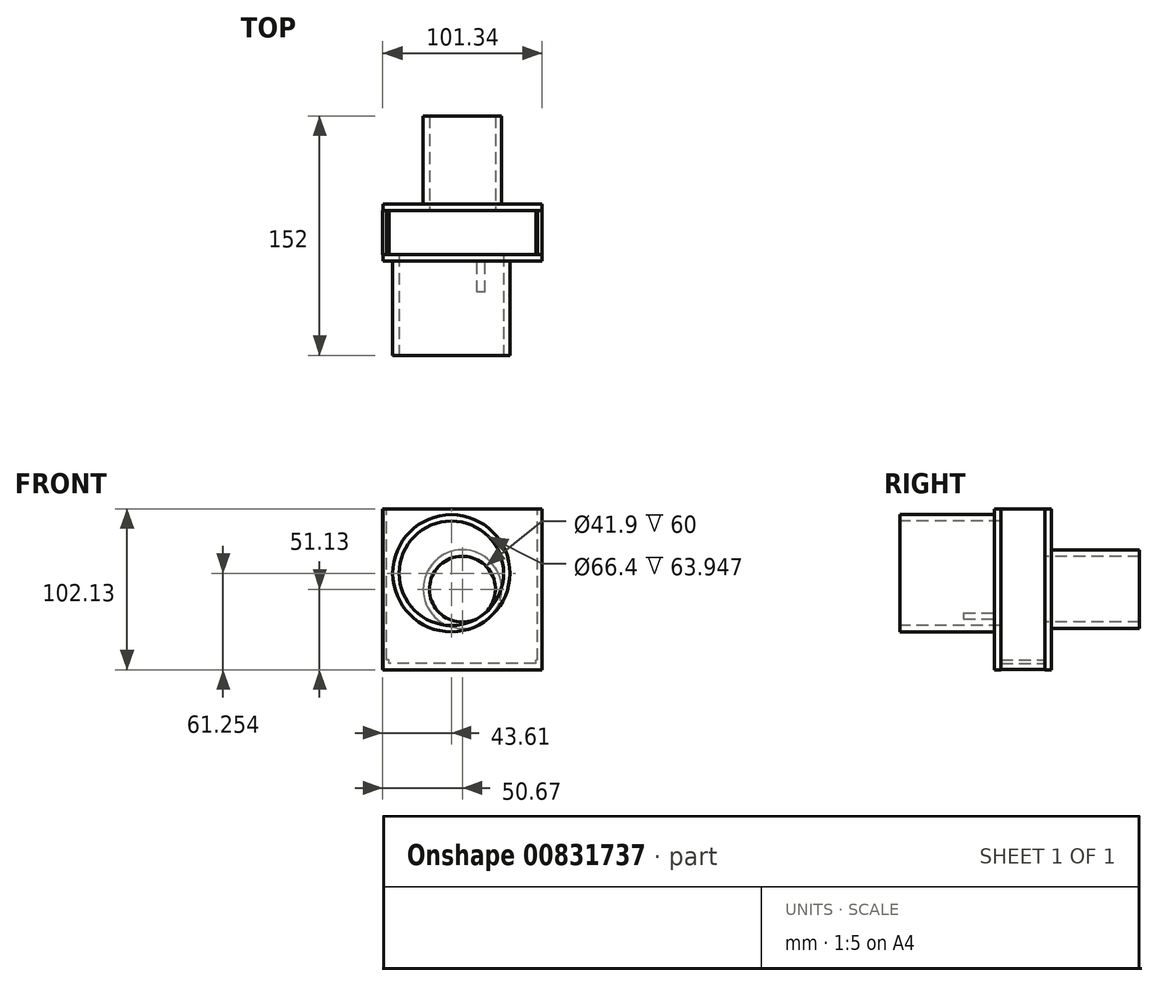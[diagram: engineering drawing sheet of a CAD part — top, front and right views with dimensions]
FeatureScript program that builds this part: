
annotation { "Feature Type Name" : "Feature", "Feature Type Description" : "" }
export const myFeature = defineFeature(function(context is Context, id is Id, definition is map)
    precondition{}
    {
        {
            var Q0;
            Q0=qCreatedBy(makeId("Front.planeOp"),FACE);
            var sketch = newSketch(context, id + "F0", { "sketchPlane" : qUnion([Q0])});
            skLineSegment(sketch, "E0.bottom", {"start": v(46.67, -47) * mm, "end": v(-46.67, -47) * mm});
            skLineSegment(sketch, "E0.top", {"start": v(46.67, 47) * mm, "end": v(-46.67, 47) * mm});
            skLineSegment(sketch, "E0.left", {"start": v(46.67, -47) * mm, "end": v(46.67, 47) * mm});
            skLineSegment(sketch, "E0.right", {"start": v(-46.67, -47) * mm, "end": v(-46.67, 47) * mm});
            skPoint(sketch, "E0.middle", {"position": v(0, 0) * mm});
            skLineSegment(sketch, "E1.0", {"start": v(50.67, 51) * mm, "end": v(-50.67, 51) * mm});
            skLineSegment(sketch, "E1.1", {"start": v(50.67, -51) * mm, "end": v(50.67, 51) * mm});
            skLineSegment(sketch, "E1.2", {"start": v(50.67, -51) * mm, "end": v(-50.67, -51) * mm});
            skLineSegment(sketch, "E1.3", {"start": v(-50.67, -51) * mm, "end": v(-50.67, 51) * mm});
            skSolve(sketch);
        }
        {
            var Q0;
            Q0=makeQuery(id+"F0.imprint","IMPRINT",FACE,{"disambiguationData":[TD([[makeQuery(id+"F0.imprint","IMPRINT",EDGE,{"derivedFrom":sQuery(id+"F0.wireOp",EDGE,"E0.bottom")}),1.0]])]});
            extrude(context, id + "F1", {"entities" : qUnion([Q0]), "depth" : 28 * mm, "offsetDistance" : 25 * mm});
        }
        {
            var Q0;
            Q0=qCreatedBy(makeId("Right.planeOp"),FACE);
            var sketch = newSketch(context, id + "F2", { "sketchPlane" : qUnion([Q0])});
            skLineSegment(sketch, "E2.bottom", {"start": v(-32, 50.87) * mm, "end": v(4, 50.87) * mm});
            skLineSegment(sketch, "E2.top", {"start": v(-32, -51.13) * mm, "end": v(4, -51.13) * mm});
            skLineSegment(sketch, "E2.left", {"start": v(-32, 50.87) * mm, "end": v(-32, -51.13) * mm});
            skLineSegment(sketch, "E2.right", {"start": v(4, 50.87) * mm, "end": v(4, -51.13) * mm});
            skLineSegment(sketch, "E3", {"start": v(-28.05, 50.87) * mm, "end": v(-28.05, -51.13) * mm});
            skLineSegment(sketch, "E4", {"start": v(-28.05, -51.13) * mm, "end": v(0, -51.13) * mm});
            skPoint(sketch, "E4.endSnap0", {"position": v(-14, -51.13) * mm});
            skLineSegment(sketch, "E5", {"start": v(0, -51.13) * mm, "end": v(0, 50.87) * mm});
            skSolve(sketch);
        }
        {
            var Q0;
            {var subQ0=sQuery(id+"F2.wireOp",EDGE,"E2.left");Q0=makeQuery(id+"F2.imprint","IMPRINT",FACE,{"disambiguationData":[TD([[makeQuery(id+"F2.imprint","IMPRINT",EDGE,{"derivedFrom":subQ0}),1.0]])]});}
            var Q1;
            {var subQ0=sQuery(id+"F2.wireOp",EDGE,"E2.right");Q1=makeQuery(id+"F2.imprint","IMPRINT",FACE,{"disambiguationData":[TD([[makeQuery(id+"F2.imprint","IMPRINT",EDGE,{"derivedFrom":subQ0}),-1.0]])]});}
            extrude(context, id + "F3", {"entities" : qUnion([Q0, Q1]), "depth" : 50.4 * mm, "offsetDistance" : 25 * mm, "hasSecondDirection" : true, "secondDirectionOppositeDirection" : true, "secondDirectionDepth" : 50.3 * mm});
        }
        {
            var Q0;
            Q0=makeQuery(id+"F1.opExtrude","SWEPT_FACE",FACE,{"disambiguationData":[OSD([sQuery(id+"F0.wireOp",EDGE,"E1.0")])]});
            var sketch = newSketch(context, id + "F4", { "sketchPlane" : qUnion([Q0])});
            skLineSegment(sketch, "E6.bottom", {"start": v(-48.2, 0) * mm, "end": v(47.8, 0) * mm});
            skLineSegment(sketch, "E6.top", {"start": v(-48.2, -28) * mm, "end": v(47.8, -28) * mm});
            skLineSegment(sketch, "E6.left", {"start": v(-48.2, 0) * mm, "end": v(-48.2, -28) * mm});
            skLineSegment(sketch, "E6.right", {"start": v(47.8, 0) * mm, "end": v(47.8, -28) * mm});
            skSolve(sketch);
        }
        {
            var Q0;
            Q0=makeQuery(id+"F4.imprint","IMPRINT",FACE,{"disambiguationData":[TD([[makeQuery(id+"F4.imprint","IMPRINT",EDGE,{"derivedFrom":sQuery(id+"F4.wireOp",EDGE,"E6.bottom")}),1.0]])]});
            extrude(context, id + "F5", {"entities" : qUnion([Q0]), "operationType" : NewBodyOperationType.REMOVE, "oppositeDirection" : true, "depth" : 96 * mm, "offsetDistance" : 25 * mm});
        }
        {
            var Q0;
            Q0=makeQuery(id+"F3.opExtrude","SWEPT_FACE",FACE,{"disambiguationData":[OSD([sQuery(id+"F2.wireOp",EDGE,"E2.left")])]});
            var sketch = newSketch(context, id + "F6", { "sketchPlane" : qUnion([Q0])});
            skLineSegment(sketch, "E7", {"start": v(-7.06, 50.87) * mm, "end": v(-7.06, -51.13) * mm});
            skLineSegment(sketch, "E8", {"start": v(-50.3, 10.12) * mm, "end": v(50.4, 10.12) * mm});
            skCircle(sketch, "E9", {"center": v(-7.06, 10.12) * mm, "radius": 33.25 * mm});
            skCircle(sketch, "E10.0", {"center": v(-7.06, 10.12) * mm, "radius": 37.25 * mm});
            skCircle(sketch, "E11", {"center": v(-7.06, 10.12) * mm, "radius": 33.2 * mm});
            skSolve(sketch);
        }
        {
            var Q0;
            {var subQ0=sQuery(id+"F6.wireOp",EDGE,"E11");var subQ1=sQuery(id+"F6.wireOp",EDGE,"E7");var subQ2=makeQuery(id+"F6.imprint","INTERSECT",VERTEX,{"disambiguationData":[OD(0.0)],"derivedFrom":[subQ1,subQ0]});Q0=makeQuery(id+"F6.imprint","IMPRINT",FACE,{"disambiguationData":[TD([[makeQuery(id+"F6.imprint","IMPRINT",EDGE,{"disambiguationData":[TD([[subQ2,-1.0]])],"derivedFrom":subQ1}),-1.0]])]});}
            var Q1;
            {var subQ0=sQuery(id+"F6.wireOp",EDGE,"E11");var subQ1=sQuery(id+"F6.wireOp",EDGE,"E7");var subQ2=makeQuery(id+"F6.imprint","INTERSECT",VERTEX,{"disambiguationData":[OD(0.0)],"derivedFrom":[subQ1,subQ0]});Q1=makeQuery(id+"F6.imprint","IMPRINT",FACE,{"disambiguationData":[TD([[makeQuery(id+"F6.imprint","IMPRINT",EDGE,{"disambiguationData":[TD([[subQ2,-1.0]])],"derivedFrom":subQ1}),1.0]])]});}
            var Q2;
            {var subQ0=sQuery(id+"F6.wireOp",EDGE,"E8");var subQ1=sQuery(id+"F6.wireOp",EDGE,"E7");var subQ2=makeQuery(id+"F6.imprint","INTERSECT",VERTEX,{"derivedFrom":[subQ1,subQ0]});Q2=makeQuery(id+"F6.imprint","IMPRINT",FACE,{"disambiguationData":[TD([[makeQuery(id+"F6.imprint","IMPRINT",EDGE,{"disambiguationData":[TD([[subQ2,-1.0]])],"derivedFrom":subQ1}),1.0]])]});}
            var Q3;
            {var subQ0=sQuery(id+"F6.wireOp",EDGE,"E8");var subQ1=sQuery(id+"F6.wireOp",EDGE,"E7");var subQ2=makeQuery(id+"F6.imprint","INTERSECT",VERTEX,{"derivedFrom":[subQ1,subQ0]});Q3=makeQuery(id+"F6.imprint","IMPRINT",FACE,{"disambiguationData":[TD([[makeQuery(id+"F6.imprint","IMPRINT",EDGE,{"disambiguationData":[TD([[subQ2,-1.0]])],"derivedFrom":subQ1}),-1.0]])]});}
            extrude(context, id + "F7", {"entities" : qUnion([Q0, Q1, Q2, Q3]), "operationType" : NewBodyOperationType.REMOVE, "oppositeDirection" : true, "depth" : 5 * mm, "offsetDistance" : 25 * mm});
        }
        {
            var Q0;
            Q0=makeQuery(id+"F3.opExtrude","SWEPT_FACE",FACE,{"disambiguationData":[OSD([sQuery(id+"F2.wireOp",EDGE,"E2.left")])]});
            var sketch = newSketch(context, id + "F8", { "sketchPlane" : qUnion([Q0])});
            skCircle(sketch, "E12.0", {"center": v(-7.06, 10.12) * mm, "radius": 37.2 * mm});
            skSolve(sketch);
        }
        {
            var Q0;
            Q0=makeQuery(id+"F8.imprint","IMPRINT",FACE,{"disambiguationData":[TD([[makeQuery(id+"F8.imprint","IMPRINT",EDGE,{"derivedFrom":sQuery(id+"F8.wireOp",EDGE,"E12.0")}),1.0]])]});
            extrude(context, id + "F9", {"entities" : qUnion([Q0]), "operationType" : NewBodyOperationType.ADD, "depth" : 60 * mm, "offsetDistance" : 25 * mm});
        }
        {
            var Q0;
            Q0=qCreatedBy(makeId("Front.planeOp"),FACE);
            var sketch = newSketch(context, id + "F10", { "sketchPlane" : qUnion([Q0])});
            skCircle(sketch, "E13", {"center": v(0, 0) * mm, "radius": 24.95 * mm});
            skCircle(sketch, "E14.0", {"center": v(0, 0) * mm, "radius": 20.95 * mm});
            skCircle(sketch, "E15", {"center": v(0, 0) * mm, "radius": 18.2 * mm});
            skSolve(sketch);
        }
        {
            var Q0;
            Q0=makeQuery(id+"F10.imprint","IMPRINT",FACE,{"disambiguationData":[TD([[makeQuery(id+"F10.imprint","IMPRINT",EDGE,{"derivedFrom":sQuery(id+"F10.wireOp",EDGE,"E13")}),1.0]])]});
            extrude(context, id + "F11", {"entities" : qUnion([Q0]), "operationType" : NewBodyOperationType.ADD, "oppositeDirection" : true, "depth" : 60 * mm, "offsetDistance" : 25 * mm});
        }
        {
            var Q0;
            Q0=makeQuery(id+"F11.boolean.opBoolean","SPLIT",FACE,{"disambiguationData":[TD([makeQuery(id+"F11.opExtrude","SWEPT_FACE",FACE,{"disambiguationData":[OSD([sQuery(id+"F10.wireOp",EDGE,"E15")])]})])],"derivedFrom":makeQuery(id+"F3.opExtrude","SWEPT_FACE",FACE,{"disambiguationData":[OSD([sQuery(id+"F2.wireOp",EDGE,"E2.right")])]})});
            var Q1;
            Q1=makeQuery(id+"F11.boolean.opBoolean","SPLIT",FACE,{"disambiguationData":[TD([makeQuery(id+"F11.opExtrude","SWEPT_FACE",FACE,{"disambiguationData":[OSD([sQuery(id+"F10.wireOp",EDGE,"E14.0")])]})])],"derivedFrom":makeQuery(id+"F3.opExtrude","SWEPT_FACE",FACE,{"disambiguationData":[OSD([sQuery(id+"F2.wireOp",EDGE,"E2.right")])]})});
            extrude(context, id + "F12", {"entities" : qUnion([Q0, Q1]), "operationType" : NewBodyOperationType.REMOVE, "oppositeDirection" : true, "depth" : 55.8 * mm, "offsetDistance" : 25 * mm});
        }
    });
